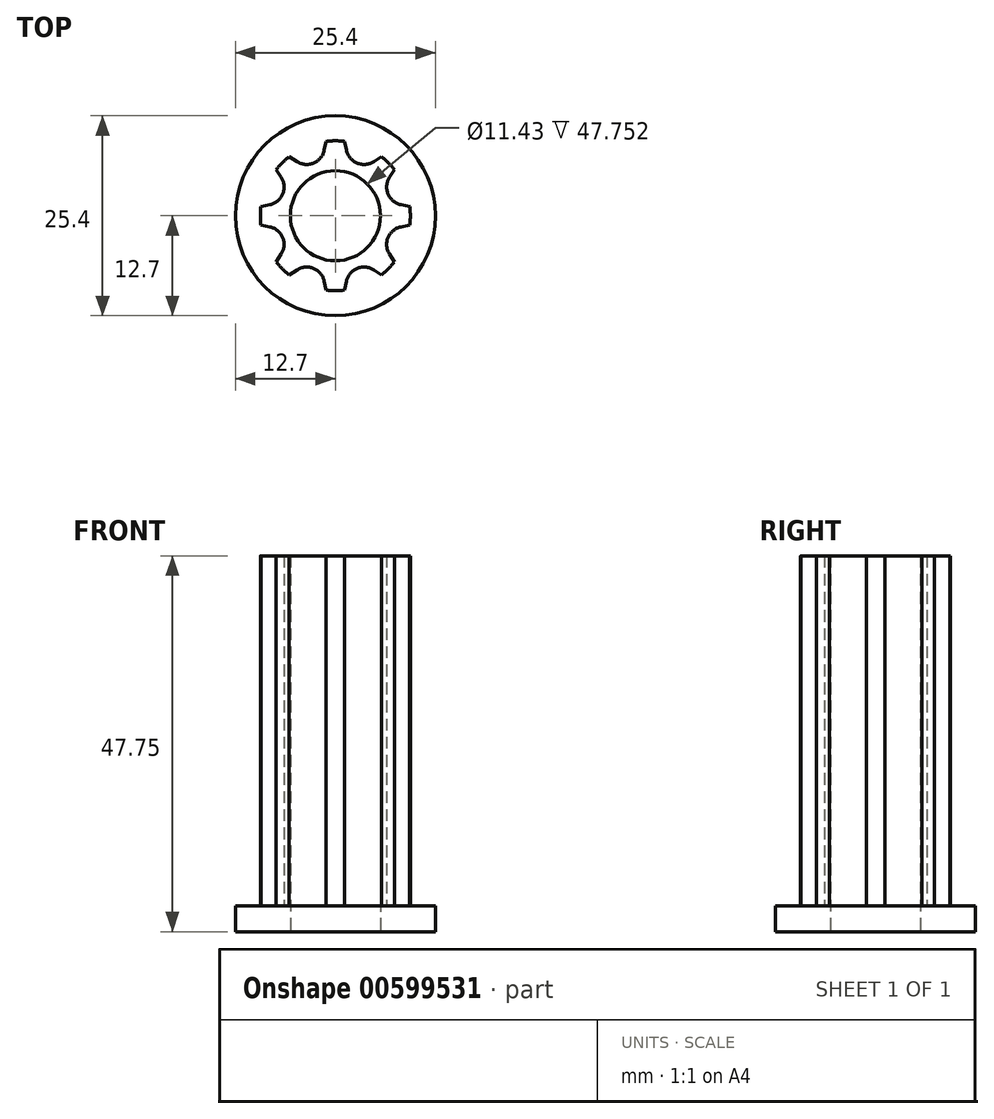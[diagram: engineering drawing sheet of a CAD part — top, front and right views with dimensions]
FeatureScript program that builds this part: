
annotation { "Feature Type Name" : "Feature", "Feature Type Description" : "" }
export const myFeature = defineFeature(function(context is Context, id is Id, definition is map)
    precondition{}
    {
        {
            var Q0;
            Q0=qCreatedBy(makeId("Top.planeOp"),FACE);
            var sketch = newSketch(context, id + "F0", { "sketchPlane" : qUnion([Q0])});
            skCircle(sketch, "E0", {"center": v(0, 0) * mm, "radius": 12.7 * mm});
            skCircle(sketch, "E1", {"center": v(0, 0) * mm, "radius": 5.72 * mm});
            skSolve(sketch);
        }
        {
            var Q0;
            Q0 = qSketchRegion(id + "F0", true);
            extrude(context, id + "F1", {"entities" : qUnion([Q0]), "depth" : 3.3 * mm, "offsetDistance" : 25.4 * mm});
        }
        {
            var Q0;
            Q0=makeQuery(id+"F1.opExtrude","CAP_FACE",FACE,{"disambiguationData":[OSD([sQuery(id+"F0.wireOp",EDGE,"E0"),sQuery(id+"F0.wireOp",EDGE,"E1")])],"isStart":false});
            var sketch = newSketch(context, id + "F2", { "sketchPlane" : qUnion([Q0])});
            skCircle(sketch, "E2", {"center": v(0, 0) * mm, "radius": 9.53 * mm});
            skLineSegment(sketch, "E3", {"start": v(0, 9.53) * mm, "end": v(0, 0) * mm});
            skCircle(sketch, "E4", {"center": v(3.65, 8.8) * mm, "radius": 2.29 * mm});
            skLineSegment(sketch, "E5", {"start": v(1.41, 8.32) * mm, "end": v(1.17, 9.45) * mm});
            skLineSegment(sketch, "E6", {"start": v(4.89, 6.88) * mm, "end": v(5.86, 7.5) * mm});
            skCircle(sketch, "E7.1.0", {"center": v(-3.64, 8.8) * mm, "radius": 2.29 * mm});
            skLineSegment(sketch, "E7.1.1", {"start": v(-4.88, 6.88) * mm, "end": v(-5.86, 7.51) * mm});
            skLineSegment(sketch, "E7.1.2", {"start": v(-1.4, 8.32) * mm, "end": v(-1.16, 9.45) * mm});
            skCircle(sketch, "E7.2.0", {"center": v(-8.8, 3.65) * mm, "radius": 2.29 * mm});
            skLineSegment(sketch, "E7.2.1", {"start": v(-8.32, 1.41) * mm, "end": v(-9.45, 1.17) * mm});
            skLineSegment(sketch, "E7.2.2", {"start": v(-6.88, 4.89) * mm, "end": v(-7.5, 5.86) * mm});
            skCircle(sketch, "E7.3.0", {"center": v(-8.8, -3.64) * mm, "radius": 2.29 * mm});
            skLineSegment(sketch, "E7.3.1", {"start": v(-6.88, -4.88) * mm, "end": v(-7.51, -5.86) * mm});
            skLineSegment(sketch, "E7.3.2", {"start": v(-8.32, -1.4) * mm, "end": v(-9.45, -1.16) * mm});
            skCircle(sketch, "E7.4.0", {"center": v(-3.65, -8.8) * mm, "radius": 2.29 * mm});
            skLineSegment(sketch, "E7.4.1", {"start": v(-1.41, -8.32) * mm, "end": v(-1.17, -9.45) * mm});
            skLineSegment(sketch, "E7.4.2", {"start": v(-4.89, -6.88) * mm, "end": v(-5.86, -7.5) * mm});
            skCircle(sketch, "E7.5.0", {"center": v(3.64, -8.8) * mm, "radius": 2.29 * mm});
            skLineSegment(sketch, "E7.5.1", {"start": v(4.88, -6.88) * mm, "end": v(5.86, -7.51) * mm});
            skLineSegment(sketch, "E7.5.2", {"start": v(1.4, -8.32) * mm, "end": v(1.16, -9.45) * mm});
            skCircle(sketch, "E7.6.0", {"center": v(8.8, -3.65) * mm, "radius": 2.29 * mm});
            skLineSegment(sketch, "E7.6.1", {"start": v(8.32, -1.41) * mm, "end": v(9.45, -1.17) * mm});
            skLineSegment(sketch, "E7.6.2", {"start": v(6.88, -4.89) * mm, "end": v(7.5, -5.86) * mm});
            skCircle(sketch, "E7.7.0", {"center": v(8.8, 3.64) * mm, "radius": 2.29 * mm});
            skLineSegment(sketch, "E7.7.1", {"start": v(6.88, 4.88) * mm, "end": v(7.51, 5.86) * mm});
            skLineSegment(sketch, "E7.7.2", {"start": v(8.32, 1.4) * mm, "end": v(9.45, 1.16) * mm});
            skSolve(sketch);
        }
        {
            var Q0;
            {var subQ12=sQuery(id+"F2.wireOp",EDGE,"E5");Q0=makeQuery(id+"F2.imprint","IMPRINT",FACE,{"disambiguationData":[TD([[makeQuery(id+"F2.imprint","IMPRINT",EDGE,{"derivedFrom":subQ12}),1.0]])]});}
            extrude(context, id + "F3", {"entities" : qUnion([Q0]), "operationType" : NewBodyOperationType.ADD, "depth" : 44.45 * mm, "offsetDistance" : 25.4 * mm});
        }
    });
